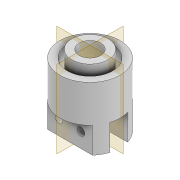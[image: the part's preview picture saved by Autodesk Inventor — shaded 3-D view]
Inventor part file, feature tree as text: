
AUTODESK INVENTOR PART (.ipt)
format: ipt  version: 2022 (Build 260153000, 153)  size: 153,600 bytes
history: native  units: mm
features: extrude x5, sketch x4, projected_geometry x1
ambient origin geometry x8: Origin, YZ Plane, XZ Plane, XY Plane, X Axis, Y Axis, Z Axis, Center Point
bodies: Solid1 (feature_tree)
feature tree (10):
  sketch  "Sketch1"  dims[d0=12.2mm d1=9.8mm]
  extrude  "Extrusion1"  Depth=9.8mm
  extrude  "Extrusion2"  Depth=3.0mm TaperAngle=0.0deg
  extrude  "Extrusion7"  Depth=10.0mm TaperAngle=0.0deg
  extrude  "Extrusion8"  Depth=3.0mm
  extrude  "Extrusion9"  Depth=4.8mm
  sketch  "Sketch7"  dims[d2=2.0mm d3=3.0mm d4=0.0mm]
  sketch  "Sketch8"  dims[d5=2.0mm d6=10.0mm d7=0.0mm]
  sketch  "Sketch9"  dims[d34=3.0mm d35=3.0mm d36=4.8mm d37=2.4mm d38=7.0mm d39=0.0mm d40=2.1mm d41=2.1mm d42=3.0mm d43=3.0mm d44=5.9mm d45=2.95mm d46=20.0mm d47=0.0mm d48=2.0mm d49=0.0mm d27=0.0mm d28=0.0mm d29=0.0mm d30=0.0mm]
  projected_geometry  "Project Cut Edges1"
